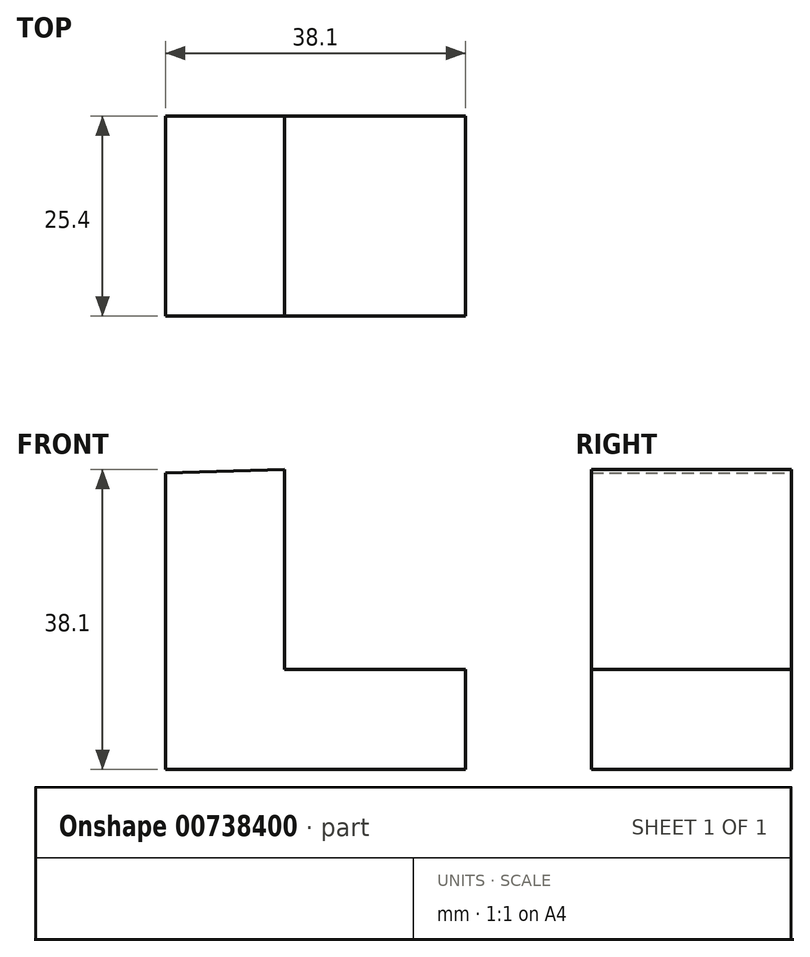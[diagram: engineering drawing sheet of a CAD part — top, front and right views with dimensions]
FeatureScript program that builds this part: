
annotation { "Feature Type Name" : "Feature", "Feature Type Description" : "" }
export const myFeature = defineFeature(function(context is Context, id is Id, definition is map)
    precondition{}
    {
        {
            var Q0;
            Q0=qCreatedBy(makeId("Front.planeOp"),FACE);
            var sketch = newSketch(context, id + "F0", { "sketchPlane" : qUnion([Q0])});
            skLineSegment(sketch, "E0", {"start": v(0, 31.75) * mm, "end": v(0, 0) * mm});
            skLineSegment(sketch, "E1", {"start": v(0, -5.9) * mm, "end": v(38.1, -5.9) * mm});
            skLineSegment(sketch, "E2", {"start": v(38.1, -5.9) * mm, "end": v(38.1, 6.8) * mm});
            skLineSegment(sketch, "E3", {"start": v(38.1, 6.8) * mm, "end": v(15.13, 6.8) * mm});
            skLineSegment(sketch, "E4", {"start": v(15.13, 6.8) * mm, "end": v(15.13, 32.2) * mm});
            skLineSegment(sketch, "E5", {"start": v(15.13, 32.2) * mm, "end": v(0, 31.75) * mm});
            skLineSegment(sketch, "E6", {"start": v(0, -5.9) * mm, "end": v(0, 0) * mm});
            skSolve(sketch);
        }
        {
            var Q0;
            Q0 = qSketchRegion(id + "F0", true);
            extrude(context, id + "F1", {"entities" : qUnion([Q0]), "depth" : 25.4 * mm, "offsetDistance" : 25.4 * mm});
        }
    });
